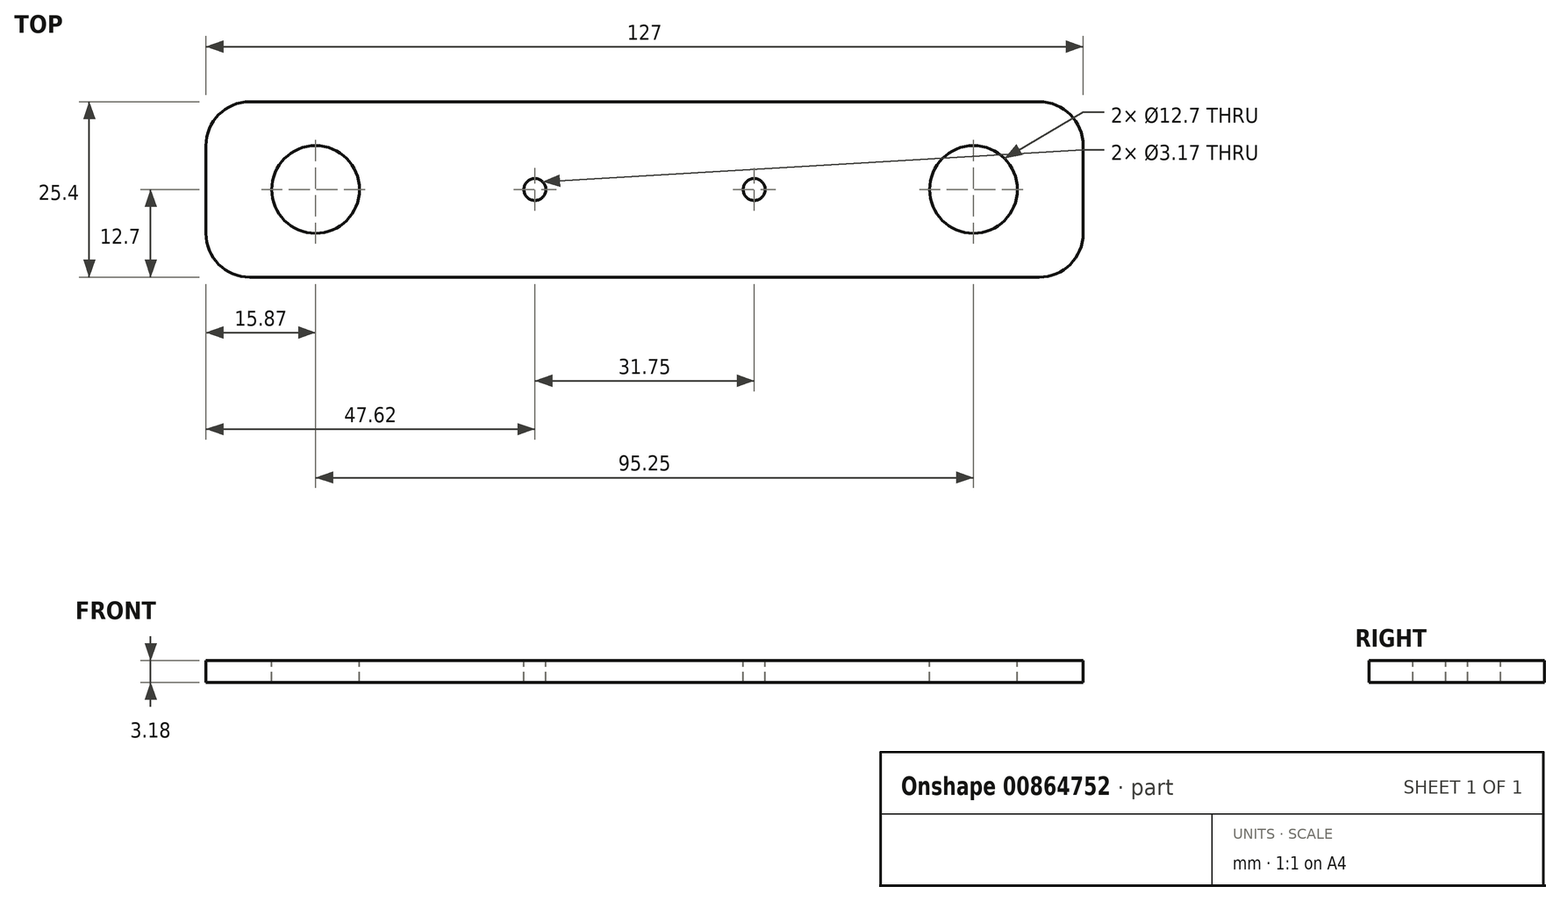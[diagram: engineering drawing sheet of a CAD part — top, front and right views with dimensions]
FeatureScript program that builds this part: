
annotation { "Feature Type Name" : "Feature", "Feature Type Description" : "" }
export const myFeature = defineFeature(function(context is Context, id is Id, definition is map)
    precondition{}
    {
        {
            var Q0;
            Q0=qCreatedBy(makeId("Top.planeOp"),FACE);
            var sketch = newSketch(context, id + "F0", { "sketchPlane" : qUnion([Q0])});
            skLineSegment(sketch, "E0.bottom", {"start": v(-101.6, 76.2) * mm, "end": v(101.6, 76.2) * mm});
            skLineSegment(sketch, "E0.top", {"start": v(-101.6, -76.2) * mm, "end": v(101.6, -76.2) * mm});
            skLineSegment(sketch, "E0.left", {"start": v(-101.6, 76.2) * mm, "end": v(-101.6, -76.2) * mm});
            skLineSegment(sketch, "E0.right", {"start": v(101.6, 76.2) * mm, "end": v(101.6, -76.2) * mm});
            skSolve(sketch);
        }
        {
            var Q0;
            Q0=makeQuery(id+"F0.imprint","IMPRINT",FACE,{"disambiguationData":[TD([[makeQuery(id+"F0.imprint","IMPRINT",EDGE,{"derivedFrom":sQuery(id+"F0.wireOp",EDGE,"E0.bottom")}),-1.0]])]});
            extrude(context, id + "F1", {"entities" : qUnion([Q0]), "depth" : 3.17 * mm, "offsetDistance" : 25.4 * mm});
        }
        {
            var Q0;
            Q0=makeQuery(id+"F1.opExtrude","CAP_FACE",FACE,{"disambiguationData":[OSD([sQuery(id+"F0.wireOp",EDGE,"E0.bottom"),sQuery(id+"F0.wireOp",EDGE,"E0.top"),sQuery(id+"F0.wireOp",EDGE,"E0.left"),sQuery(id+"F0.wireOp",EDGE,"E0.right")])],"isStart":false});
            var sketch = newSketch(context, id + "F2", { "sketchPlane" : qUnion([Q0])});
            skCircle(sketch, "E1", {"center": v(-31.75, 0) * mm, "radius": 65.66 * mm});
            skCircle(sketch, "E2", {"center": v(63.5, 0) * mm, "radius": 33.9 * mm});
            skCircle(sketch, "E3", {"center": v(63.5, 0) * mm, "radius": 31.75 * mm});
            skCircle(sketch, "E4", {"center": v(-31.75, 0) * mm, "radius": 63.5 * mm});
            skCircle(sketch, "E5", {"center": v(-31.75, 0) * mm, "radius": 6.35 * mm});
            skCircle(sketch, "E6", {"center": v(63.5, 0) * mm, "radius": 6.35 * mm});
            skSolve(sketch);
        }
        {
            var Q0;
            Q0=makeQuery(id+"F2.imprint","IMPRINT",FACE,{"disambiguationData":[TD([[makeQuery(id+"F2.imprint","IMPRINT",EDGE,{"derivedFrom":sQuery(id+"F2.wireOp",EDGE,"E5")}),1.0]])]});
            var Q1;
            Q1=makeQuery(id+"F2.imprint","IMPRINT",FACE,{"disambiguationData":[TD([[makeQuery(id+"F2.imprint","IMPRINT",EDGE,{"derivedFrom":sQuery(id+"F2.wireOp",EDGE,"E6")}),1.0]])]});
            extrude(context, id + "F3", {"entities" : qUnion([Q0, Q1]), "operationType" : NewBodyOperationType.REMOVE, "endBound" : BoundingType.THROUGH_ALL, "oppositeDirection" : true, "depth" : 25.4 * mm, "offsetDistance" : 25.4 * mm});
        }
        {
            var Q0;
            Q0=makeQuery(id+"F1.opExtrude","CAP_FACE",FACE,{"disambiguationData":[OSD([sQuery(id+"F0.wireOp",EDGE,"E0.bottom"),sQuery(id+"F0.wireOp",EDGE,"E0.top"),sQuery(id+"F0.wireOp",EDGE,"E0.left"),sQuery(id+"F0.wireOp",EDGE,"E0.right")])],"isStart":false});
            var sketch = newSketch(context, id + "F4", { "sketchPlane" : qUnion([Q0])});
            skLineSegment(sketch, "E7.bottom", {"start": v(-47.63, 12.7) * mm, "end": v(79.38, 12.7) * mm});
            skLineSegment(sketch, "E7.top", {"start": v(-47.63, -12.7) * mm, "end": v(79.38, -12.7) * mm});
            skLineSegment(sketch, "E7.left", {"start": v(-47.63, 12.7) * mm, "end": v(-47.63, -12.7) * mm});
            skLineSegment(sketch, "E7.right", {"start": v(79.38, 12.7) * mm, "end": v(79.38, -12.7) * mm});
            skSolve(sketch);
        }
        {
            var Q0;
            Q0=makeQuery(id+"F4.imprint","IMPRINT",FACE,{"disambiguationData":[TD([[makeQuery(id+"F4.imprint","IMPRINT",EDGE,{"derivedFrom":sQuery(id+"F4.wireOp",EDGE,"E7.bottom")}),1.0]])]});
            extrude(context, id + "F5", {"entities" : qUnion([Q0]), "operationType" : NewBodyOperationType.REMOVE, "endBound" : BoundingType.THROUGH_ALL, "oppositeDirection" : true, "depth" : 25.4 * mm, "offsetDistance" : 25.4 * mm});
        }
        {
            var Q0;
            Q0=makeQuery(id+"F5.boolean.opBoolean","COPY",EDGE,{"derivedFrom":makeQuery(id+"F5.opExtrude","SWEPT_EDGE",EDGE,{"disambiguationData":[OSD([sQuery(id+"F4.wireOp",EDGE,"E7.bottom"),sQuery(id+"F4.wireOp",EDGE,"E7.left")])]})});
            var Q1;
            Q1=makeQuery(id+"F5.boolean.opBoolean","COPY",EDGE,{"derivedFrom":makeQuery(id+"F5.opExtrude","SWEPT_EDGE",EDGE,{"disambiguationData":[OSD([sQuery(id+"F4.wireOp",EDGE,"E7.top"),sQuery(id+"F4.wireOp",EDGE,"E7.left")])]})});
            var Q2;
            Q2=makeQuery(id+"F5.boolean.opBoolean","COPY",EDGE,{"derivedFrom":makeQuery(id+"F5.opExtrude","SWEPT_EDGE",EDGE,{"disambiguationData":[OSD([sQuery(id+"F4.wireOp",EDGE,"E7.top"),sQuery(id+"F4.wireOp",EDGE,"E7.right")])]})});
            var Q3;
            Q3=makeQuery(id+"F5.boolean.opBoolean","COPY",EDGE,{"derivedFrom":makeQuery(id+"F5.opExtrude","SWEPT_EDGE",EDGE,{"disambiguationData":[OSD([sQuery(id+"F4.wireOp",EDGE,"E7.bottom"),sQuery(id+"F4.wireOp",EDGE,"E7.right")])]})});
            fillet(context, id + "F6", {"entities" : qUnion([Q0, Q1, Q2, Q3]), "radius" : 6.35 * mm, "tangentPropagation" : true, "allowEdgeOverflow" : false});
        }
        {
            var Q0;
            Q0=makeQuery(id+"F1.opExtrude","CAP_FACE",FACE,{"disambiguationData":[OSD([sQuery(id+"F0.wireOp",EDGE,"E0.bottom"),sQuery(id+"F0.wireOp",EDGE,"E0.top"),sQuery(id+"F0.wireOp",EDGE,"E0.left"),sQuery(id+"F0.wireOp",EDGE,"E0.right")])],"isStart":false});
            var sketch = newSketch(context, id + "F7", { "sketchPlane" : qUnion([Q0])});
            skCircle(sketch, "E8", {"center": v(0, 0) * mm, "radius": 1.59 * mm});
            skCircle(sketch, "E9", {"center": v(31.75, 0) * mm, "radius": 1.59 * mm});
            skSolve(sketch);
        }
        {
            var Q0;
            Q0=makeQuery(id+"F7.imprint","IMPRINT",FACE,{"disambiguationData":[TD([[makeQuery(id+"F7.imprint","IMPRINT",EDGE,{"derivedFrom":sQuery(id+"F7.wireOp",EDGE,"E8")}),1.0]])]});
            var Q1;
            Q1=makeQuery(id+"F7.imprint","IMPRINT",FACE,{"disambiguationData":[TD([[makeQuery(id+"F7.imprint","IMPRINT",EDGE,{"derivedFrom":sQuery(id+"F7.wireOp",EDGE,"E9")}),1.0]])]});
            extrude(context, id + "F8", {"entities" : qUnion([Q0, Q1]), "operationType" : NewBodyOperationType.REMOVE, "endBound" : BoundingType.THROUGH_ALL, "oppositeDirection" : true, "depth" : 25.4 * mm, "offsetDistance" : 25.4 * mm});
        }
    });
